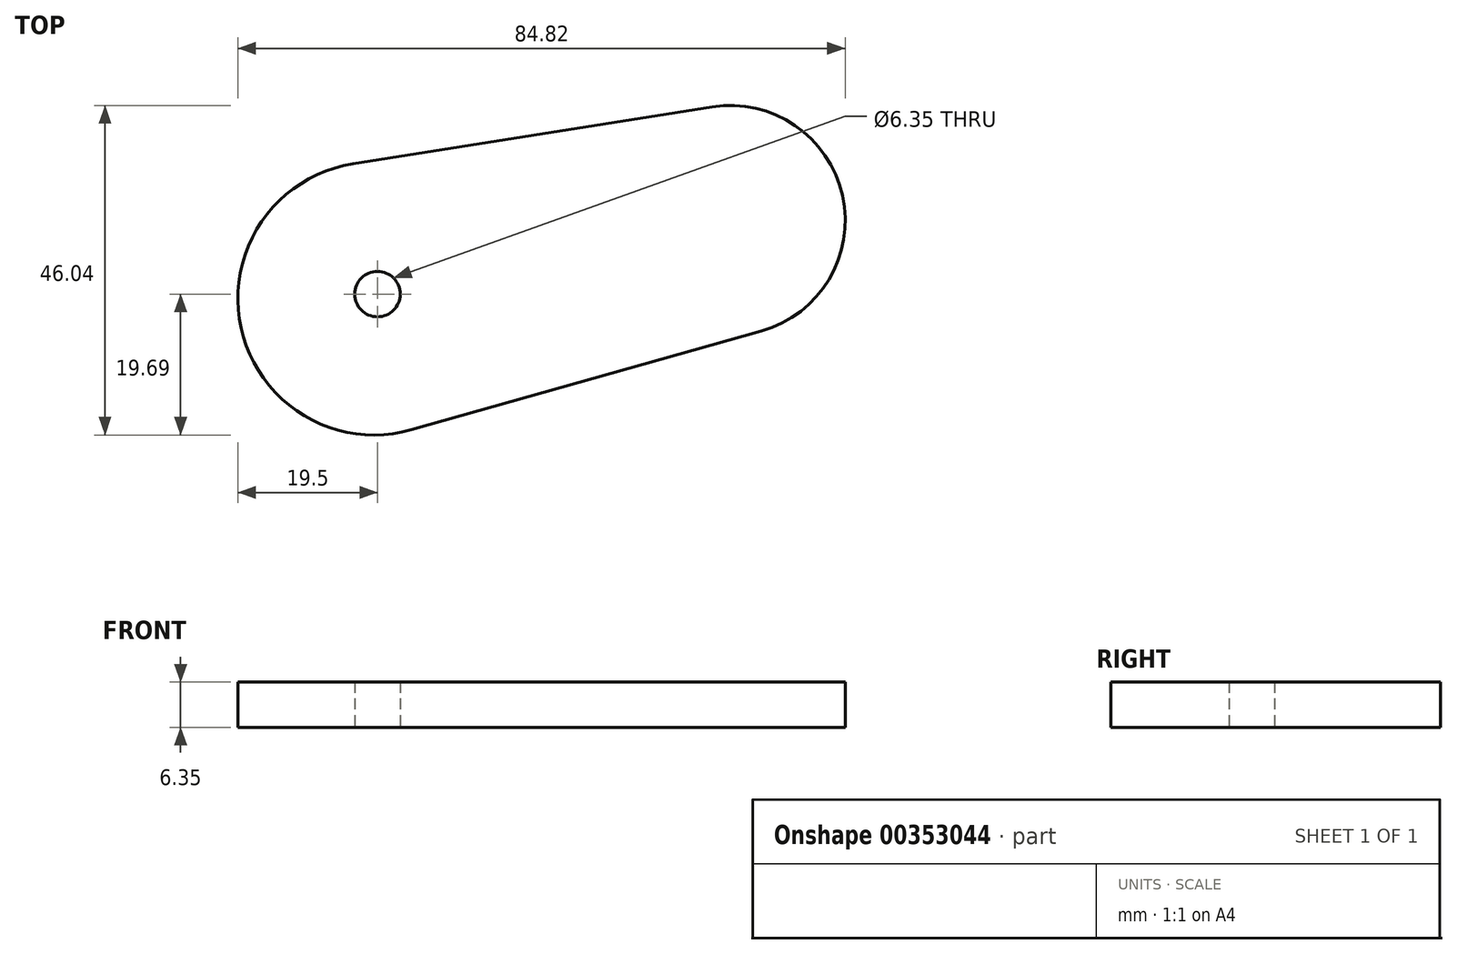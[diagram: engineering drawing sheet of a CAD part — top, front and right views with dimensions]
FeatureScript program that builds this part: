
annotation { "Feature Type Name" : "Feature", "Feature Type Description" : "" }
export const myFeature = defineFeature(function(context is Context, id is Id, definition is map)
    precondition{}
    {
        {
            var Q0;
            Q0=qCreatedBy(makeId("Top.planeOp"),FACE);
            var sketch = newSketch(context, id + "F0", { "sketchPlane" : qUnion([Q0])});
            skLineSegment(sketch, "E0", {"start": v(4.72, -18.97) * mm, "end": v(53.62, -5.18) * mm});
            skArc(sketch, "E1", {"start": v(53.62, -5.18) * mm, "mid": v(64.94, 13.74) * mm, "end": v(46.73, 26.16) * mm});
            skLineSegment(sketch, "E2", {"start": v(-3.44, 18.18) * mm, "end": v(46.73, 26.16) * mm});
            skCircle(sketch, "E3", {"center": v(0, 0) * mm, "radius": 3.18 * mm});
            skArc(sketch, "E4", {"start": v(-3.44, 18.18) * mm, "mid": v(-19.05, -4.73) * mm, "end": v(4.72, -18.97) * mm});
            skLineSegment(sketch, "E5", {"start": v(0, 0) * mm, "end": v(14, 0) * mm, "construction": true});
            skLineSegment(sketch, "E6", {"start": v(-3.44, 18.18) * mm, "end": v(-3.05, 11.83) * mm});
            skCircle(sketch, "E7", {"center": v(188.41, 49.62) * mm, "radius": 3.05 * mm});
            skSolve(sketch);
        }
        {
            var Q0;
            Q0=makeQuery(id+"F0.imprint","IMPRINT",FACE,{"disambiguationData":[TD([[makeQuery(id+"F0.imprint","IMPRINT",EDGE,{"derivedFrom":sQuery(id+"F0.wireOp",EDGE,"E0")}),1.0]])]});
            extrude(context, id + "F1", {"entities" : qUnion([Q0]), "depth" : 6.35 * mm});
        }
        {
            var Q0;
            Q0=makeQuery(id+"F0.imprint","IMPRINT",FACE,{"disambiguationData":[TD([[makeQuery(id+"F0.imprint","IMPRINT",EDGE,{"derivedFrom":sQuery(id+"F0.wireOp",EDGE,"E0")}),1.0]])]});
            extrude(context, id + "F2", {"entities" : qUnion([Q0]), "operationType" : NewBodyOperationType.ADD, "depth" : 6.35 * mm});
        }
    });
